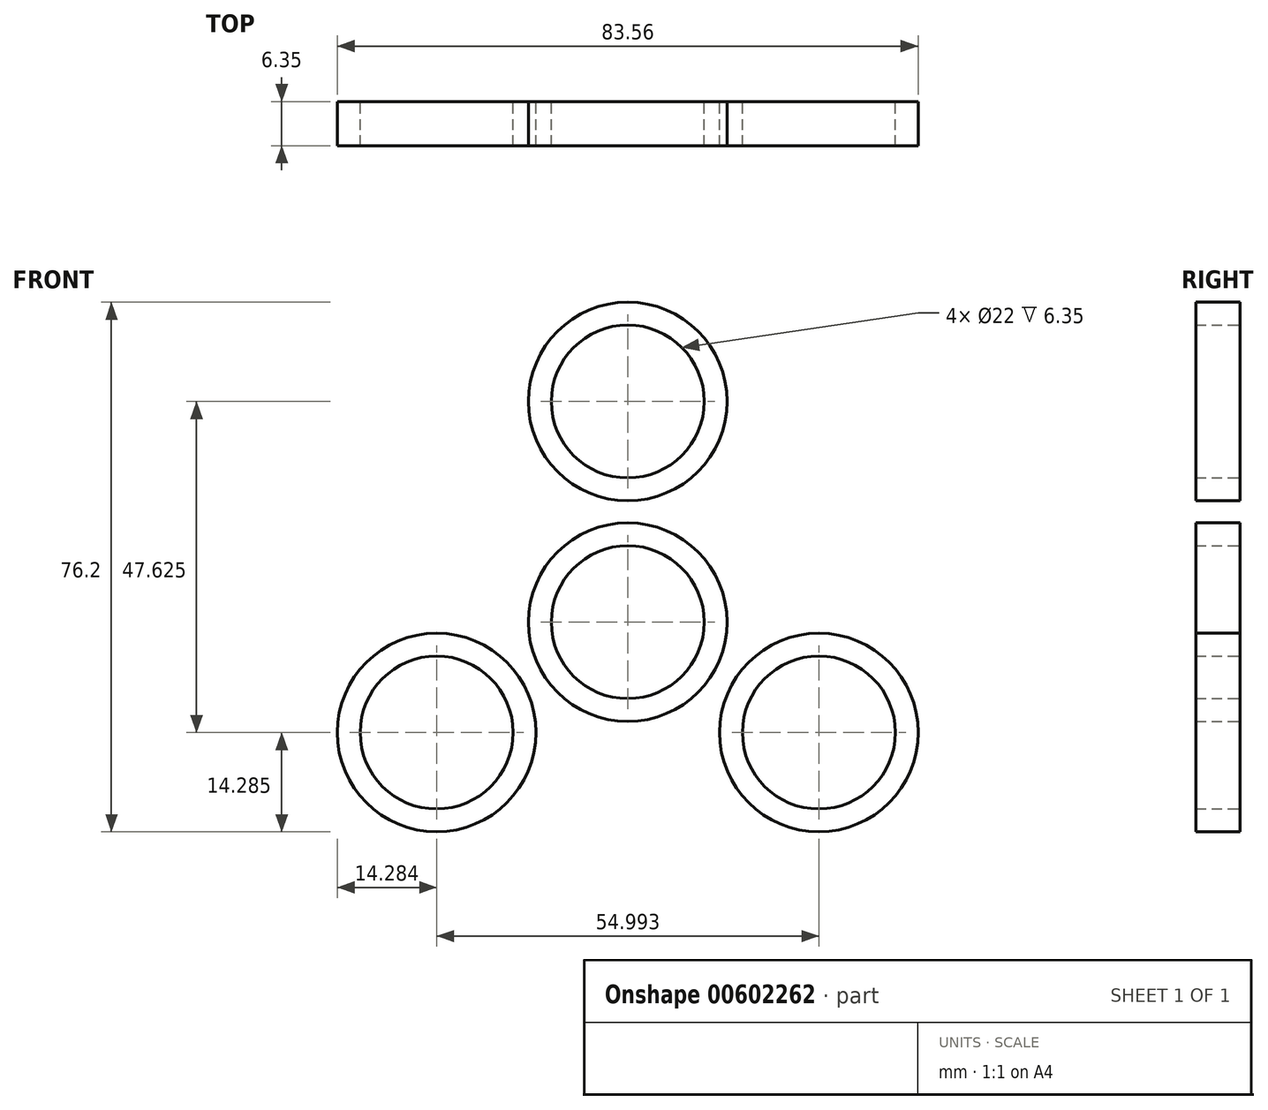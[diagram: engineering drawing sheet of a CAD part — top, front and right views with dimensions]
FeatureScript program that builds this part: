
annotation { "Feature Type Name" : "Feature", "Feature Type Description" : "" }
export const myFeature = defineFeature(function(context is Context, id is Id, definition is map)
    precondition{}
    {
        {
            var Q0;
            Q0=qCreatedBy(makeId("Front.planeOp"),FACE);
            var sketch = newSketch(context, id + "F0", { "sketchPlane" : qUnion([Q0])});
            skCircle(sketch, "E0", {"center": v(0, 0) * mm, "radius": 14.29 * mm});
            skCircle(sketch, "E1", {"center": v(0, 0) * mm, "radius": 11 * mm});
            skCircle(sketch, "E2", {"center": v(0, 31.75) * mm, "radius": 14.29 * mm});
            skCircle(sketch, "E3", {"center": v(0, 31.75) * mm, "radius": 11 * mm});
            skCircle(sketch, "E4.1.0", {"center": v(-27.5, -15.87) * mm, "radius": 14.29 * mm});
            skCircle(sketch, "E4.1.1", {"center": v(-27.5, -15.87) * mm, "radius": 11 * mm});
            skCircle(sketch, "E4.2.0", {"center": v(27.5, -15.88) * mm, "radius": 14.29 * mm});
            skCircle(sketch, "E4.2.1", {"center": v(27.5, -15.88) * mm, "radius": 11 * mm});
            skCircle(sketch, "E5", {"center": v(0, 0) * mm, "radius": 31.75 * mm});
            skSolve(sketch);
        }
        {
            var Q0;
            {var subQ0=sQuery(id+"F0.wireOp",EDGE,"E5");var subQ1=sQuery(id+"F0.wireOp",EDGE,"E4.1.0");var subQ2=makeQuery(id+"F0.imprint","INTERSECT",VERTEX,{"disambiguationData":[OD(0.0)],"derivedFrom":[subQ1,subQ0]});Q0=makeQuery(id+"F0.imprint","IMPRINT",FACE,{"disambiguationData":[TD([[makeQuery(id+"F0.imprint","IMPRINT",EDGE,{"disambiguationData":[TD([[subQ2,-1.0]])],"derivedFrom":subQ1}),1.0]])]});}
            var Q1;
            {var subQ0=sQuery(id+"F0.wireOp",EDGE,"E5");var subQ1=sQuery(id+"F0.wireOp",EDGE,"E4.1.0");var subQ2=makeQuery(id+"F0.imprint","INTERSECT",VERTEX,{"disambiguationData":[OD(0.0)],"derivedFrom":[subQ1,subQ0]});Q1=makeQuery(id+"F0.imprint","IMPRINT",FACE,{"disambiguationData":[TD([[makeQuery(id+"F0.imprint","IMPRINT",EDGE,{"disambiguationData":[TD([[subQ2,1.0]])],"derivedFrom":subQ1}),1.0]])]});}
            var Q2;
            {var subQ0=sQuery(id+"F0.wireOp",EDGE,"E5");var subQ1=sQuery(id+"F0.wireOp",EDGE,"E2");var subQ2=makeQuery(id+"F0.imprint","INTERSECT",VERTEX,{"disambiguationData":[OD(0.0)],"derivedFrom":[subQ1,subQ0]});Q2=makeQuery(id+"F0.imprint","IMPRINT",FACE,{"disambiguationData":[TD([[makeQuery(id+"F0.imprint","IMPRINT",EDGE,{"disambiguationData":[TD([[subQ2,1.0]])],"derivedFrom":subQ1}),1.0]])]});}
            var Q3;
            {var subQ0=sQuery(id+"F0.wireOp",EDGE,"E5");var subQ1=sQuery(id+"F0.wireOp",EDGE,"E2");var subQ2=makeQuery(id+"F0.imprint","INTERSECT",VERTEX,{"disambiguationData":[OD(0.0)],"derivedFrom":[subQ1,subQ0]});Q3=makeQuery(id+"F0.imprint","IMPRINT",FACE,{"disambiguationData":[TD([[makeQuery(id+"F0.imprint","IMPRINT",EDGE,{"disambiguationData":[TD([[subQ2,-1.0]])],"derivedFrom":subQ1}),1.0]])]});}
            var Q4;
            Q4=makeQuery(id+"F0.imprint","IMPRINT",FACE,{"disambiguationData":[TD([[makeQuery(id+"F0.imprint","IMPRINT",EDGE,{"derivedFrom":sQuery(id+"F0.wireOp",EDGE,"E0")}),1.0]])]});
            var Q5;
            {var subQ0=sQuery(id+"F0.wireOp",EDGE,"E5");var subQ1=sQuery(id+"F0.wireOp",EDGE,"E4.2.0");var subQ2=makeQuery(id+"F0.imprint","INTERSECT",VERTEX,{"disambiguationData":[OD(0.0)],"derivedFrom":[subQ1,subQ0]});Q5=makeQuery(id+"F0.imprint","IMPRINT",FACE,{"disambiguationData":[TD([[makeQuery(id+"F0.imprint","IMPRINT",EDGE,{"disambiguationData":[TD([[subQ2,1.0]])],"derivedFrom":subQ1}),1.0]])]});}
            var Q6;
            {var subQ0=sQuery(id+"F0.wireOp",EDGE,"E5");var subQ1=sQuery(id+"F0.wireOp",EDGE,"E4.2.0");var subQ2=makeQuery(id+"F0.imprint","INTERSECT",VERTEX,{"disambiguationData":[OD(0.0)],"derivedFrom":[subQ1,subQ0]});Q6=makeQuery(id+"F0.imprint","IMPRINT",FACE,{"disambiguationData":[TD([[makeQuery(id+"F0.imprint","IMPRINT",EDGE,{"disambiguationData":[TD([[subQ2,-1.0]])],"derivedFrom":subQ1}),1.0]])]});}
            extrude(context, id + "F1", {"entities" : qUnion([Q0, Q1, Q2, Q3, Q4, Q5, Q6]), "depth" : 6.35 * mm, "offsetDistance" : 25.4 * mm});
        }
    });
